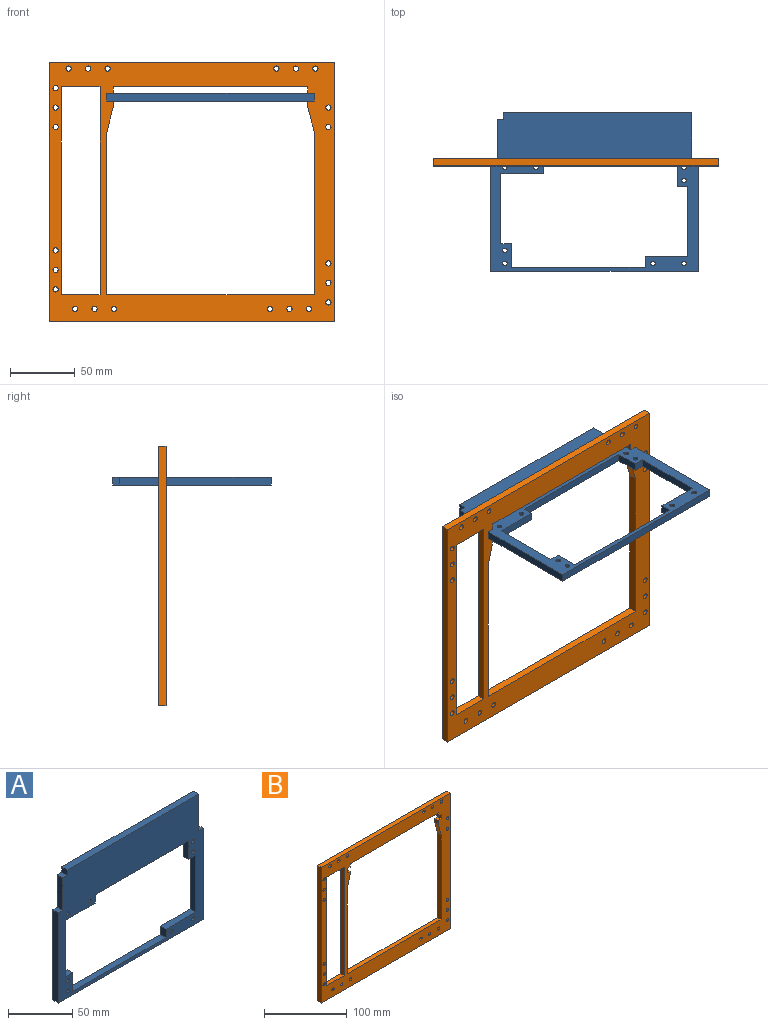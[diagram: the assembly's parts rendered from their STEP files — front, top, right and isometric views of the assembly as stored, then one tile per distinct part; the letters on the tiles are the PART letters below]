
ASSEMBLY  parts=2 mates=1
PART A: 32 faces, bbox 160x6x122 mm
  f0: plane 6x5mm, normal (0,0,1), area 30mm2, adj f17,f21,f22,f31
  f1: plane 54x6mm, normal (-1,0,0), area 324mm2, adj f2,f20,f21,f22
  f2: plane 33x6mm, normal (0,0,1), area 198mm2, adj f1,f3,f21,f22
  f3: plane 8x6mm, normal (-1,0,0), area 48mm2, adj f2,f4,f21,f22
  f4: plane 103x6mm, normal (0,0,1), area 618mm2, adj f3,f5,f21,f22
  f5: plane 18x6mm, normal (1,0,0), area 108mm2, adj f4,f6,f21,f22
  f6: plane 8x6mm, normal (0,0,1), area 48mm2, adj f5,f7,f21,f22
  f7: plane 54x6mm, normal (1,0,0), area 324mm2, adj f6,f8,f21,f22
  f8: plane 33x6mm, normal (0,0,-1), area 198mm2, adj f7,f9,f21,f22
  f9: plane 8x6mm, normal (1,0,0), area 48mm2, adj f8,f10,f21,f22
  f10: plane 103x6mm, normal (0,0,-1), area 618mm2, adj f9,f11,f21,f22
  f11: plane 18x6mm, normal (-1,0,0), area 108mm2, adj f10,f20,f21,f22
  f12: plane 6x5mm, normal (0,0,1), area 30mm2, adj f13,f19,f21,f22
  f13: plane 31x6mm, normal (-1,0,0), area 186mm2, adj f12,f14,f21,f22
  f14: plane 6x5mm, normal (0,0,1), area 30mm2, adj f13,f15,f21,f22
  f15: plane 86x6mm, normal (-1,0,0), area 516mm2, adj f14,f16,f21,f22
  f16: plane 160x6mm, normal (0,0,-1), area 960mm2, adj f15,f17,f21,f22
  f17: plane 87x6mm, normal (1,0,0), area 522mm2, adj f0,f16,f21,f22
  f18: plane 145x6mm, normal (0,0,1), area 870mm2, adj f19,f21,f22,f31
  f19: plane 6x5mm, normal (-1,0,0), area 30mm2, adj f12,f18,f21,f22
  f20: plane 8x6mm, normal (0,0,-1), area 48mm2, adj f1,f11,f21,f22
  f21: plane 160x122mm, normal (0,-1,0), area 8358.8mm2, adj f0,f1,f2,f3,f4,f5,f6,f7
  f22: plane 160x122mm, normal (0,1,0), area 8358.8mm2, adj f0,f1,f2,f3,f4,f5,f6,f7
  f23: cylinder r=1.75mm len=6mm, axis (0,1,0), area 66.1mm2, adj f21,f22
  f24: cylinder r=1.75mm len=6mm, axis (0,1,0), area 66.1mm2, adj f21,f22
  f25: cylinder r=1.75mm len=6mm, axis (0,1,0), area 66.1mm2, adj f21,f22
  f26: cylinder r=1.75mm len=6mm, axis (0,1,0), area 66.1mm2, adj f21,f22
  f27: cylinder r=1.75mm len=6mm, axis (0,1,0), area 66.1mm2, adj f21,f22
  f28: cylinder r=1.75mm len=6mm, axis (0,1,0), area 66.1mm2, adj f21,f22
  f29: cylinder r=1.75mm len=6mm, axis (0,1,0), area 66.1mm2, adj f21,f22
  f30: cylinder r=1.75mm len=6mm, axis (0,1,0), area 66.1mm2, adj f21,f22
  f31: plane 35x6mm, normal (1,0,0), area 210mm2, adj f0,f18,f21,f22
PART B: 49 faces, bbox 220x6x200 mm
  f0: plane 160x6mm, normal (0,0,1), area 960mm2, adj f1,f23,f24,f25
  f1: plane 124x6mm, normal (1,0,0), area 744mm2, adj f0,f2,f24,f25
  f2: plane 20x6mm, normal (0.97,0,-0.24), area 123.7mm2, adj f1,f3,f24,f25
  f3: plane 6x5mm, normal (1,0,0), area 30mm2, adj f2,f4,f24,f25
  f4: plane 6x5mm, normal (0,0,1), area 30mm2, adj f3,f5,f24,f25
  f5: plane 6x6mm, normal (1,0,0), area 36mm2, adj f4,f6,f24,f25
  f6: plane 6x5mm, normal (0,0,-1), area 30mm2, adj f5,f7,f24,f25
  f7: plane 6x5mm, normal (1,0,0), area 30mm2, adj f6,f8,f24,f25
  f8: plane 150x6mm, normal (0,0,-1), area 900mm2, adj f7,f9,f24,f25
  f9: plane 6x5mm, normal (-1,0,0), area 30mm2, adj f8,f10,f24,f25
  f10: plane 6x5mm, normal (0,0,-1), area 30mm2, adj f9,f11,f24,f25
  f11: plane 6x6mm, normal (-1,0,0), area 36mm2, adj f10,f12,f24,f25
  f12: plane 6x5mm, normal (0,0,1), area 30mm2, adj f11,f13,f24,f25
  f13: plane 6x5mm, normal (-1,0,0), area 30mm2, adj f12,f14,f24,f25
  f14: plane 19x6mm, normal (-0.97,0,-0.25), area 117.9mm2, adj f13,f23,f24,f25
  f15: plane 160x6mm, normal (-1,0,0), area 960mm2, adj f16,f21,f24,f25
  f16: plane 30x6mm, normal (0,0,1), area 180mm2, adj f15,f17,f24,f25
  f17: plane 160x6mm, normal (1,0,0), area 960mm2, adj f16,f21,f24,f25
  f18: plane 200x6mm, normal (-1,0,0), area 1200mm2, adj f19,f22,f24,f25
  f19: plane 220x6mm, normal (0,0,-1), area 1320mm2, adj f18,f20,f24,f25
  f20: plane 200x6mm, normal (1,0,0), area 1200mm2, adj f19,f22,f24,f25
  f21: plane 30x6mm, normal (0,0,-1), area 180mm2, adj f15,f17,f24,f25
  f22: plane 220x6mm, normal (0,0,1), area 1320mm2, adj f18,f20,f24,f25
  f23: plane 125x6mm, normal (-1,0,0), area 750mm2, adj f0,f14,f24,f25
  f24: plane 220x200mm, normal (0,-1,0), area 13508.5mm2, adj f0,f1,f2,f3,f4,f5,f6,f7
  f25: plane 220x200mm, normal (0,1,0), area 13508.5mm2, adj f0,f1,f2,f3,f4,f5,f6,f7
  f26: cylinder r=2mm len=6mm, axis (0,1,0), area 75.4mm2, adj f24,f25
  f27: cylinder r=2mm len=6mm, axis (0,1,0), area 75.4mm2, adj f24,f25
  f28: cylinder r=2mm len=6mm, axis (0,1,0), area 75.4mm2, adj f24,f25
  f29: cylinder r=2mm len=6mm, axis (0,1,0), area 75.4mm2, adj f24,f25
  f30: cylinder r=2mm len=6mm, axis (0,1,0), area 75.4mm2, adj f24,f25
  f31: cylinder r=2mm len=6mm, axis (0,1,0), area 75.4mm2, adj f24,f25
  f32: cylinder r=2mm len=6mm, axis (0,1,0), area 75.4mm2, adj f24,f25
  f33: cylinder r=2mm len=6mm, axis (0,1,0), area 75.4mm2, adj f24,f25
  f34: cylinder r=2mm len=6mm, axis (0,1,0), area 75.4mm2, adj f24,f25
  f35: cylinder r=2mm len=6mm, axis (0,1,0), area 75.4mm2, adj f24,f25
  f36: cylinder r=2mm len=6mm, axis (0,1,0), area 75.4mm2, adj f24,f25
  f37: cylinder r=2mm len=6mm, axis (0,1,0), area 75.4mm2, adj f24,f25
  f38: cylinder r=2mm len=6mm, axis (0,1,0), area 75.4mm2, adj f24,f25
  f39: cylinder r=2mm len=6mm, axis (0,1,0), area 75.4mm2, adj f24,f25
  f40: cylinder r=2mm len=6mm, axis (0,1,0), area 75.4mm2, adj f24,f25
  f41: cylinder r=2mm len=6mm, axis (0,1,0), area 75.4mm2, adj f24,f25
  f42: cylinder r=2mm len=6mm, axis (0,1,0), area 75.4mm2, adj f24,f25
  f43: cylinder r=2mm len=6mm, axis (0,1,0), area 75.4mm2, adj f24,f25
  f44: cylinder r=2mm len=6mm, axis (0,1,0), area 75.4mm2, adj f24,f25
  f45: cylinder r=2mm len=6mm, axis (0,1,0), area 75.4mm2, adj f24,f25
  f46: cylinder r=2mm len=6mm, axis (0,1,0), area 75.4mm2, adj f24,f25
  f47: cylinder r=2mm len=6mm, axis (0,1,0), area 75.4mm2, adj f24,f25
  f48: cylinder r=2mm len=6mm, axis (0,1,0), area 75.4mm2, adj f24,f25
PLACE A rot(axis=(-1,0,0),90deg) t=(-110,-46,-30)mm
PLACE B t=(-110,0,-100)mm
MATE fastened A.f0 <-> B.f25  axis (0,1,0) through (-15.81,0,-27)mm
